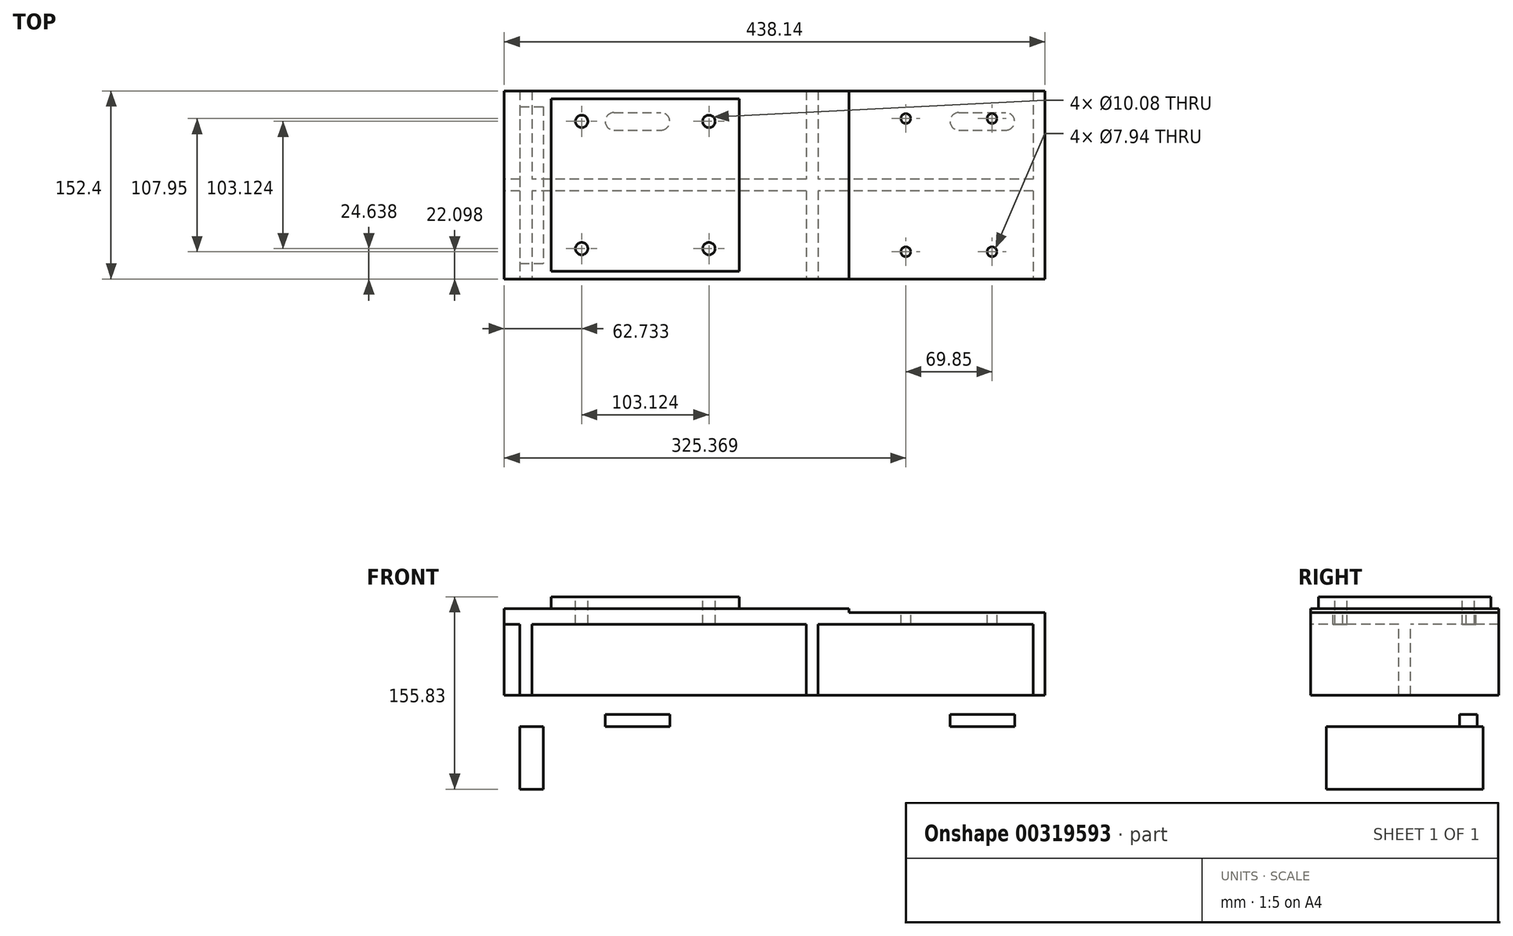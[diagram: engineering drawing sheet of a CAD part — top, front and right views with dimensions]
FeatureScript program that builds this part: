
annotation { "Feature Type Name" : "Feature", "Feature Type Description" : "" }
export const myFeature = defineFeature(function(context is Context, id is Id, definition is map)
    precondition{}
    {
        {
            var Q0;
            Q0=qCreatedBy(makeId("Top.planeOp"),FACE);
            var sketch = newSketch(context, id + "F0", { "sketchPlane" : qUnion([Q0])});
            skLineSegment(sketch, "E0.bottom", {"start": v(-219.08, 76.2) * mm, "end": v(219.08, 76.2) * mm});
            skLineSegment(sketch, "E0.top", {"start": v(-219.08, -76.2) * mm, "end": v(219.07, -76.2) * mm});
            skLineSegment(sketch, "E0.left", {"start": v(-219.08, 76.2) * mm, "end": v(-219.08, -76.2) * mm});
            skLineSegment(sketch, "E0.right", {"start": v(219.08, 76.2) * mm, "end": v(219.07, -76.2) * mm});
            skPoint(sketch, "E0.middle", {"position": v(0, 0) * mm});
            skSolve(sketch);
        }
        {
            var Q0;
            Q0 = qSketchRegion(id + "F0", true);
            extrude(context, id + "F1", {"entities" : qUnion([Q0]), "oppositeDirection" : true, "depth" : 12.7 * mm});
        }
        {
            var Q0;
            Q0=makeQuery(id+"F1.opExtrude","CAP_FACE",FACE,{"disambiguationData":[OSD([sQuery(id+"F0.wireOp",EDGE,"E0.bottom"),sQuery(id+"F0.wireOp",EDGE,"E0.top"),sQuery(id+"F0.wireOp",EDGE,"E0.left"),sQuery(id+"F0.wireOp",EDGE,"E0.right")])],"isStart":true});
            var sketch = newSketch(context, id + "F2", { "sketchPlane" : qUnion([Q0])});
            skLineSegment(sketch, "E1.0", {"start": v(-104.78, 76.2) * mm, "end": v(-104.78, -76.2) * mm, "construction": true});
            skLineSegment(sketch, "E2.bottom", {"start": v(-180.98, -69.85) * mm, "end": v(-28.58, -69.85) * mm});
            skLineSegment(sketch, "E2.top", {"start": v(-180.98, 69.85) * mm, "end": v(-28.58, 69.85) * mm});
            skLineSegment(sketch, "E2.left", {"start": v(-180.98, -69.85) * mm, "end": v(-180.98, 69.85) * mm});
            skLineSegment(sketch, "E2.right", {"start": v(-28.58, -69.85) * mm, "end": v(-28.58, 69.85) * mm});
            skPoint(sketch, "E2.middle", {"position": v(-104.78, 0) * mm});
            skSolve(sketch);
        }
        {
            var Q0;
            Q0 = qSketchRegion(id + "F2", true);
            extrude(context, id + "F3", {"entities" : qUnion([Q0]), "operationType" : NewBodyOperationType.ADD, "depth" : 9.52 * mm});
        }
        {
            var Q0;
            Q0=makeQuery(id+"F1.opExtrude","CAP_FACE",FACE,{"disambiguationData":[OSD([sQuery(id+"F0.wireOp",EDGE,"E0.bottom"),sQuery(id+"F0.wireOp",EDGE,"E0.top"),sQuery(id+"F0.wireOp",EDGE,"E0.left"),sQuery(id+"F0.wireOp",EDGE,"E0.right")])],"isStart":false});
            var sketch = newSketch(context, id + "F4", { "sketchPlane" : qUnion([Q0])});
            skLineSegment(sketch, "E3.0", {"start": v(-206.38, 76.2) * mm, "end": v(-196.72, 76.2) * mm});
            skLineSegment(sketch, "E4.0", {"start": v(-206.38, -76.2) * mm, "end": v(-196.72, -76.2) * mm});
            skLineSegment(sketch, "E5.0", {"start": v(-206.38, -76.2) * mm, "end": v(-206.38, 76.2) * mm});
            skLineSegment(sketch, "E6.0", {"start": v(-196.72, -76.2) * mm, "end": v(-196.72, 76.2) * mm});
            skLineSegment(sketch, "E7.0", {"start": v(25.53, -76.2) * mm, "end": v(25.53, 76.2) * mm});
            skLineSegment(sketch, "E8.0", {"start": v(35.18, -76.2) * mm, "end": v(35.18, 76.2) * mm});
            skLineSegment(sketch, "E9.0", {"start": v(219.08, -76.2) * mm, "end": v(219.07, 76.2) * mm});
            skLineSegment(sketch, "E10.0", {"start": v(209.42, -76.2) * mm, "end": v(209.42, 76.2) * mm});
            skLineSegment(sketch, "E11", {"start": v(219.08, 0) * mm, "end": v(-321.3, 0) * mm, "construction": true});
            skPoint(sketch, "E11.endSnap0", {"position": v(219.07, 0) * mm});
            skLineSegment(sketch, "E12.0", {"start": v(219.08, 4.76) * mm, "end": v(-219.08, 4.76) * mm});
            skLineSegment(sketch, "E13.MirrorCS", {"start": v(219.08, -4.76) * mm, "end": v(-219.08, -4.76) * mm});
            skLineSegment(sketch, "E14.0", {"start": v(-219.08, -4.76) * mm, "end": v(-219.08, 4.76) * mm});
            skPoint(sketch, "E15.orphan", {"position": v(-219.08, 76.2) * mm});
            skPoint(sketch, "E16.orphan", {"position": v(-321.3, 4.76) * mm});
            skPoint(sketch, "E17.orphan", {"position": v(-321.3, -4.76) * mm});
            skPoint(sketch, "E18.orphan", {"position": v(-219.08, -76.2) * mm});
            skLineSegment(sketch, "E19.trimOffspring", {"start": v(25.53, -76.2) * mm, "end": v(35.18, -76.2) * mm});
            skLineSegment(sketch, "E20.trimOffspring", {"start": v(25.53, 76.2) * mm, "end": v(35.18, 76.2) * mm});
            skLineSegment(sketch, "E21.trimOffspring", {"start": v(209.42, 76.2) * mm, "end": v(219.07, 76.2) * mm});
            skLineSegment(sketch, "E22.trimOffspring", {"start": v(209.42, -76.2) * mm, "end": v(219.08, -76.2) * mm});
            skSolve(sketch);
        }
        {
            var Q0;
            Q0 = qSketchRegion(id + "F4", true);
            extrude(context, id + "F5", {"entities" : qUnion([Q0]), "operationType" : NewBodyOperationType.ADD, "depth" : 73.15 * mm});
        }
        {
            var Q0;
            Q0=makeQuery(id+"F5.opExtrude","CAP_FACE",FACE,{"disambiguationData":[OSD([sQuery(id+"F4.wireOp",EDGE,"E3.0"),sQuery(id+"F4.wireOp",EDGE,"E4.0"),sQuery(id+"F4.wireOp",EDGE,"E5.0"),sQuery(id+"F4.wireOp",EDGE,"E6.0"),sQuery(id+"F4.wireOp",EDGE,"E7.0"),sQuery(id+"F4.wireOp",EDGE,"E8.0"),sQuery(id+"F4.wireOp",EDGE,"E9.0"),sQuery(id+"F4.wireOp",EDGE,"E10.0"),sQuery(id+"F4.wireOp",EDGE,"E12.0"),sQuery(id+"F4.wireOp",EDGE,"E13.MirrorCS"),sQuery(id+"F4.wireOp",EDGE,"E14.0"),sQuery(id+"F4.wireOp",EDGE,"E19.trimOffspring"),sQuery(id+"F4.wireOp",EDGE,"E20.trimOffspring"),sQuery(id+"F4.wireOp",EDGE,"E21.trimOffspring"),sQuery(id+"F4.wireOp",EDGE,"E22.trimOffspring")])],"isStart":false});
            var sketch = newSketch(context, id + "F6", { "sketchPlane" : qUnion([Q0])});
            skLineSegment(sketch, "E23.0", {"start": v(-219.08, 76.2) * mm, "end": v(219.07, 76.2) * mm});
            skLineSegment(sketch, "E24.0", {"start": v(-219.08, -76.2) * mm, "end": v(-219.08, 76.2) * mm});
            skLineSegment(sketch, "E25.0", {"start": v(-219.08, -76.2) * mm, "end": v(219.08, -76.2) * mm});
            skLineSegment(sketch, "E26.0", {"start": v(219.08, -76.2) * mm, "end": v(219.07, 76.2) * mm});
            skPoint(sketch, "E27.orphan", {"position": v(-219.08, -4.76) * mm});
            skPoint(sketch, "E28.orphan", {"position": v(-196.72, 76.2) * mm});
            skPoint(sketch, "E29.orphan", {"position": v(25.53, 76.2) * mm});
            skPoint(sketch, "E30.orphan", {"position": v(-196.72, -76.2) * mm});
            skPoint(sketch, "E31.orphan", {"position": v(25.53, -76.2) * mm});
            skSolve(sketch);
        }
        {
            var Q0;
            Q0 = qSketchRegion(id + "F6", true);
            extrude(context, id + "F7", {"entities" : qUnion([Q0]), "operationType" : NewBodyOperationType.ADD, "depth" : 9.65 * mm});
        }
        {
            var Q0;
            Q0=makeQuery(id+"F7.opExtrude","CAP_FACE",FACE,{"disambiguationData":[OSD([sQuery(id+"F6.wireOp",EDGE,"E23.0"),sQuery(id+"F6.wireOp",EDGE,"E24.0"),sQuery(id+"F6.wireOp",EDGE,"E25.0"),sQuery(id+"F6.wireOp",EDGE,"E26.0")])],"isStart":false});
            var sketch = newSketch(context, id + "F8", { "sketchPlane" : qUnion([Q0])});
            skLineSegment(sketch, "E32", {"start": v(-219.08, 0) * mm, "end": v(219.07, 0) * mm, "construction": true});
            skLineSegment(sketch, "E33.0", {"start": v(-130.18, -76.2) * mm, "end": v(-130.18, 76.2) * mm, "construction": true});
            skLineSegment(sketch, "E34.0", {"start": v(-92.08, -76.2) * mm, "end": v(-92.08, 76.2) * mm, "construction": true});
            skLineSegment(sketch, "E35.0", {"start": v(149.22, -76.2) * mm, "end": v(149.22, 76.2) * mm, "construction": true});
            skLineSegment(sketch, "E36.0", {"start": v(187.32, -76.2) * mm, "end": v(187.32, 76.2) * mm, "construction": true});
            skLineSegment(sketch, "E37.0", {"start": v(-130.18, -51.56) * mm, "end": v(-92.08, -51.56) * mm});
            skLineSegment(sketch, "E38.trimOffspring", {"start": v(149.22, -51.56) * mm, "end": v(187.32, -51.56) * mm});
            skArc(sketch, "E39.0.startCap", {"start": v(-130.18, -58.67) * mm, "mid": v(-137.29, -51.56) * mm, "end": v(-130.18, -44.45) * mm});
            skArc(sketch, "E39.0.endCap", {"start": v(-92.08, -44.45) * mm, "mid": v(-84.96, -51.56) * mm, "end": v(-92.08, -58.67) * mm});
            skLineSegment(sketch, "E39.0.left", {"start": v(-130.18, -44.45) * mm, "end": v(-92.08, -44.45) * mm});
            skLineSegment(sketch, "E39.0.right", {"start": v(-130.18, -58.67) * mm, "end": v(-92.08, -58.67) * mm});
            skArc(sketch, "E39.1.startCap", {"start": v(149.22, -58.67) * mm, "mid": v(142.11, -51.56) * mm, "end": v(149.22, -44.45) * mm});
            skArc(sketch, "E39.1.endCap", {"start": v(187.32, -44.45) * mm, "mid": v(194.44, -51.56) * mm, "end": v(187.32, -58.67) * mm});
            skLineSegment(sketch, "E39.1.left", {"start": v(149.22, -44.45) * mm, "end": v(187.32, -44.45) * mm});
            skLineSegment(sketch, "E39.1.right", {"start": v(149.22, -58.67) * mm, "end": v(187.32, -58.67) * mm});
            skArc(sketch, "E40.MirrorCS", {"start": v(-92.08, 44.45) * mm, "mid": v(-84.96, 51.56) * mm, "end": v(-92.08, 58.67) * mm});
            skArc(sketch, "E41.MirrorCS", {"start": v(-130.18, 58.67) * mm, "mid": v(-137.29, 51.56) * mm, "end": v(-130.18, 44.45) * mm});
            skLineSegment(sketch, "E42.MirrorCS", {"start": v(149.22, 51.56) * mm, "end": v(187.32, 51.56) * mm});
            skLineSegment(sketch, "E43.MirrorCS", {"start": v(-130.18, 51.56) * mm, "end": v(-92.08, 51.56) * mm});
            skLineSegment(sketch, "E44.MirrorCS", {"start": v(149.22, 58.67) * mm, "end": v(187.32, 58.67) * mm});
            skLineSegment(sketch, "E45.MirrorCS", {"start": v(-130.18, 44.45) * mm, "end": v(-92.08, 44.45) * mm});
            skLineSegment(sketch, "E46.MirrorCS", {"start": v(149.22, 44.45) * mm, "end": v(187.32, 44.45) * mm});
            skArc(sketch, "E47.MirrorCS", {"start": v(149.22, 58.67) * mm, "mid": v(142.11, 51.56) * mm, "end": v(149.22, 44.45) * mm});
            skArc(sketch, "E48.MirrorCS", {"start": v(187.32, 44.45) * mm, "mid": v(194.44, 51.56) * mm, "end": v(187.32, 58.67) * mm});
            skLineSegment(sketch, "E49.MirrorCS", {"start": v(-130.18, 58.67) * mm, "end": v(-92.08, 58.67) * mm});
            skSolve(sketch);
        }
        {
            var Q0;
            Q0=makeQuery(id+"F8.imprint","IMPRINT",FACE,{"disambiguationData":[TD([[makeQuery(id+"F8.imprint","IMPRINT",EDGE,{"derivedFrom":sQuery(id+"F8.wireOp",EDGE,"E40.MirrorCS")}),1.0]])]});
            var Q1;
            Q1=makeQuery(id+"F8.imprint","IMPRINT",FACE,{"disambiguationData":[TD([[makeQuery(id+"F8.imprint","IMPRINT",EDGE,{"derivedFrom":sQuery(id+"F8.wireOp",EDGE,"E39.0.startCap")}),-1.0]])]});
            var Q2;
            Q2=makeQuery(id+"F8.imprint","IMPRINT",FACE,{"disambiguationData":[TD([[makeQuery(id+"F8.imprint","IMPRINT",EDGE,{"derivedFrom":sQuery(id+"F8.wireOp",EDGE,"E44.MirrorCS")}),-1.0]])]});
            var Q3;
            Q3=makeQuery(id+"F8.imprint","IMPRINT",FACE,{"disambiguationData":[TD([[makeQuery(id+"F8.imprint","IMPRINT",EDGE,{"derivedFrom":sQuery(id+"F8.wireOp",EDGE,"E39.1.startCap")}),-1.0]])]});
            extrude(context, id + "F9", {"entities" : qUnion([Q0, Q1, Q2, Q3]), "operationType" : NewBodyOperationType.REMOVE, "oppositeDirection" : true, "depth" : 25.4 * mm});
        }
        {
            var Q0;
            Q0=makeQuery(id+"F3.opExtrude","CAP_FACE",FACE,{"disambiguationData":[OSD([sQuery(id+"F2.wireOp",EDGE,"E2.bottom"),sQuery(id+"F2.wireOp",EDGE,"E2.top"),sQuery(id+"F2.wireOp",EDGE,"E2.left"),sQuery(id+"F2.wireOp",EDGE,"E2.right")])],"isStart":false});
            var sketch = newSketch(context, id + "F10", { "sketchPlane" : qUnion([Q0])});
            skLineSegment(sketch, "E50.0", {"start": v(-180.98, 69.85) * mm, "end": v(-28.58, 69.85) * mm, "construction": true});
            skLineSegment(sketch, "E51.0", {"start": v(-180.98, -69.85) * mm, "end": v(-180.98, 69.85) * mm, "construction": true});
            skLineSegment(sketch, "E52.0", {"start": v(-180.98, -69.85) * mm, "end": v(-28.58, -69.85) * mm, "construction": true});
            skLineSegment(sketch, "E53", {"start": v(-28.58, -69.85) * mm, "end": v(-180.97, 69.85) * mm, "construction": true});
            skLineSegment(sketch, "E54.bottom", {"start": v(-156.34, 51.56) * mm, "end": v(-53.21, 51.56) * mm, "construction": true});
            skLineSegment(sketch, "E54.top", {"start": v(-156.34, -51.56) * mm, "end": v(-53.21, -51.56) * mm, "construction": true});
            skLineSegment(sketch, "E54.left", {"start": v(-156.34, 51.56) * mm, "end": v(-156.34, -51.56) * mm, "construction": true});
            skLineSegment(sketch, "E54.right", {"start": v(-53.21, 51.56) * mm, "end": v(-53.21, -51.56) * mm, "construction": true});
            skPoint(sketch, "E54.middle", {"position": v(-104.78, 0) * mm});
            skPoint(sketch, "E55", {"position": v(-156.34, 51.56) * mm});
            skPoint(sketch, "E56", {"position": v(-53.21, 51.56) * mm});
            skPoint(sketch, "E57", {"position": v(-156.34, -51.56) * mm});
            skPoint(sketch, "E58", {"position": v(-53.21, -51.56) * mm});
            skSolve(sketch);
        }
        {
            var Q0;
            Q0=sQuery(id+"F10.wireOp",VERTEX,"E55");
            var Q1;
            Q1=sQuery(id+"F10.wireOp",VERTEX,"E56");
            var Q2;
            Q2=sQuery(id+"F10.wireOp",VERTEX,"E57");
            var Q3;
            Q3=sQuery(id+"F10.wireOp",VERTEX,"E58");
            var Q4;
            Q4=makeQuery(id+"F1.opExtrude","SWEPT_BODY",BODY,{"disambiguationData":[OSD([sQuery(id+"F0.wireOp",EDGE,"E0.bottom"),sQuery(id+"F0.wireOp",EDGE,"E0.top"),sQuery(id+"F0.wireOp",EDGE,"E0.left"),sQuery(id+"F0.wireOp",EDGE,"E0.right")])]});
            hole(context, id + "F11", {"style" : HoleStyle.SIMPLE, "endStyle" : HoleEndStyle.BLIND, "standardTappedOrClearance" : lookupTablePath({ "standard" : "ANSI", "fit" : "Normal (ASME)", "size" : "3/8", "type" : "Clearance" }), "standardBlindInLast" : lookupTablePath({ "fit" : "Free", "standard" : "ANSI", "size" : "3/8", "type" : "Clearance" }), "holeDiameter" : 10.08 * mm, "holeDepth" : 38.1 * mm, "tappedDepth" : 14.3 * mm, "tapClearance" : 3, "locations" : qUnion([Q0, Q1, Q2, Q3]), "scope" : qUnion([Q4])});
        }
        {
            var Q0;
            Q0=makeQuery(id+"F1.opExtrude","CAP_FACE",FACE,{"disambiguationData":[OSD([sQuery(id+"F0.wireOp",EDGE,"E0.bottom"),sQuery(id+"F0.wireOp",EDGE,"E0.top"),sQuery(id+"F0.wireOp",EDGE,"E0.left"),sQuery(id+"F0.wireOp",EDGE,"E0.right")])],"isStart":true});
            var sketch = newSketch(context, id + "F12", { "sketchPlane" : qUnion([Q0])});
            skLineSegment(sketch, "E59.bottom", {"start": v(219.08, 76.2) * mm, "end": v(60.33, 76.2) * mm});
            skLineSegment(sketch, "E59.top", {"start": v(219.08, -76.2) * mm, "end": v(60.33, -76.2) * mm});
            skLineSegment(sketch, "E59.left", {"start": v(219.08, 76.2) * mm, "end": v(219.08, -76.2) * mm});
            skLineSegment(sketch, "E59.right", {"start": v(60.33, 76.2) * mm, "end": v(60.33, -76.2) * mm});
            skSolve(sketch);
        }
        {
            var Q0;
            Q0 = qSketchRegion(id + "F12", true);
            extrude(context, id + "F13", {"entities" : qUnion([Q0]), "operationType" : NewBodyOperationType.REMOVE, "oppositeDirection" : true, "depth" : 3.17 * mm});
        }
        {
            var Q0;
            Q0=makeQuery(id+"F13.boolean.opBoolean","COPY",FACE,{"derivedFrom":makeQuery(id+"F13.opExtrude","CAP_FACE",FACE,{"disambiguationData":[OSD([sQuery(id+"F12.wireOp",EDGE,"E59.bottom"),sQuery(id+"F12.wireOp",EDGE,"E59.top"),sQuery(id+"F12.wireOp",EDGE,"E59.left"),sQuery(id+"F12.wireOp",EDGE,"E59.right")])],"isStart":false})});
            var sketch = newSketch(context, id + "F14", { "sketchPlane" : qUnion([Q0])});
            skLineSegment(sketch, "E60.0", {"start": v(-180.98, 69.85) * mm, "end": v(-28.58, 69.85) * mm, "construction": true});
            skLineSegment(sketch, "E61", {"start": v(-104.78, 69.85) * mm, "end": v(-104.78, -100.76) * mm, "construction": true});
            skLineSegment(sketch, "E62.0", {"start": v(219.08, 76.2) * mm, "end": v(219.07, -76.2) * mm, "construction": true});
            skLineSegment(sketch, "E63", {"start": v(219.07, 0) * mm, "end": v(-246.08, 0) * mm, "construction": true});
            skLineSegment(sketch, "E64.0", {"start": v(141.35, 69.85) * mm, "end": v(141.35, -100.76) * mm, "construction": true});
            skLineSegment(sketch, "E65.0", {"start": v(106.3, 69.85) * mm, "end": v(106.3, -100.76) * mm, "construction": true});
            skLineSegment(sketch, "E66.0", {"start": v(219.07, 53.85) * mm, "end": v(-246.08, 53.85) * mm, "construction": true});
            skPoint(sketch, "E67", {"position": v(106.3, 53.85) * mm});
            skPoint(sketch, "E68.0.1.0", {"position": v(106.3, -54.1) * mm});
            skPoint(sketch, "E68.1.0.0", {"position": v(176.15, 53.85) * mm});
            skPoint(sketch, "E68.1.1.0", {"position": v(176.15, -54.1) * mm});
            skLineSegment(sketch, "E68.direction1", {"start": v(106.3, 53.85) * mm, "end": v(176.15, 53.85) * mm, "construction": true});
            skLineSegment(sketch, "E68.direction2", {"start": v(106.3, 53.85) * mm, "end": v(106.3, -54.1) * mm, "construction": true});
            skSolve(sketch);
        }
        {
            var Q0;
            Q0=sQuery(id+"F14.wireOp",VERTEX,"E67");
            var Q1;
            Q1=sQuery(id+"F14.wireOp",VERTEX,"E68.1.0.0");
            var Q2;
            Q2=sQuery(id+"F14.wireOp",VERTEX,"E68.1.1.0");
            var Q3;
            Q3=sQuery(id+"F14.wireOp",VERTEX,"E68.0.1.0");
            var Q4;
            Q4=makeQuery(id+"F1.opExtrude","SWEPT_BODY",BODY,{"disambiguationData":[OSD([sQuery(id+"F0.wireOp",EDGE,"E0.bottom"),sQuery(id+"F0.wireOp",EDGE,"E0.top"),sQuery(id+"F0.wireOp",EDGE,"E0.left"),sQuery(id+"F0.wireOp",EDGE,"E0.right")])]});
            hole(context, id + "F15", {"style" : HoleStyle.SIMPLE, "endStyle" : HoleEndStyle.BLIND, "holeDiameter" : 7.94 * mm, "holeDepth" : 38.1 * mm, "tappedDepth" : 14.3 * mm, "tapClearance" : 3, "locations" : qUnion([Q0, Q1, Q2, Q3]), "scope" : qUnion([Q4])});
        }
        {
            var Q0;
            Q0=makeQuery(id+"F7.opExtrude","CAP_FACE",FACE,{"disambiguationData":[OSD([sQuery(id+"F6.wireOp",EDGE,"E23.0"),sQuery(id+"F6.wireOp",EDGE,"E24.0"),sQuery(id+"F6.wireOp",EDGE,"E25.0"),sQuery(id+"F6.wireOp",EDGE,"E26.0")])],"isStart":false});
            var sketch = newSketch(context, id + "F16", { "sketchPlane" : qUnion([Q0])});
            skLineSegment(sketch, "E69.0", {"start": v(-206.38, -63.5) * mm, "end": v(-206.38, 63.5) * mm});
            skLineSegment(sketch, "E70.0", {"start": v(-187.33, -63.5) * mm, "end": v(-187.33, 63.5) * mm});
            skLineSegment(sketch, "E71", {"start": v(-219.08, 0) * mm, "end": v(-163.17, 0) * mm, "construction": true});
            skPoint(sketch, "E71.endSnap0", {"position": v(-219.08, 0) * mm});
            skLineSegment(sketch, "E72.0", {"start": v(-206.38, -63.5) * mm, "end": v(-187.33, -63.5) * mm});
            skLineSegment(sketch, "E73.MirrorCS", {"start": v(-206.38, 63.5) * mm, "end": v(-187.33, 63.5) * mm});
            skPoint(sketch, "E74.orphan", {"position": v(-219.08, 63.5) * mm});
            skPoint(sketch, "E75.orphan", {"position": v(-163.17, 63.5) * mm});
            skPoint(sketch, "E76.orphan", {"position": v(-163.17, -63.5) * mm});
            skPoint(sketch, "E77.orphan", {"position": v(-219.08, -63.5) * mm});
            skSolve(sketch);
        }
        {
            var Q0;
            Q0 = qSketchRegion(id + "F16", true);
            extrude(context, id + "F17", {"entities" : qUnion([Q0]), "operationType" : NewBodyOperationType.ADD, "depth" : 50.8 * mm});
        }
        {
            var Q0;
            Q0=makeQuery(id+"F17.opExtrude","SWEPT_FACE",FACE,{"disambiguationData":[OSD([sQuery(id+"F16.wireOp",EDGE,"E69.0")])]});
            var sketch = newSketch(context, id + "F18", { "sketchPlane" : qUnion([Q0])});
            skLineSegment(sketch, "E78.0", {"start": v(-76.2, -127.25) * mm, "end": v(76.2, -127.25) * mm, "construction": true});
            skLineSegment(sketch, "E79", {"start": v(0, -146.3) * mm, "end": v(0, -111.54) * mm, "construction": true});
            skPoint(sketch, "E79.endSnap0", {"position": v(0, -127.25) * mm});
            skLineSegment(sketch, "E80.0", {"start": v(50.8, -146.3) * mm, "end": v(50.8, -111.54) * mm, "construction": true});
            skPoint(sketch, "E81", {"position": v(50.8, -127.25) * mm});
            skPoint(sketch, "E82.MirrorP", {"position": v(-50.8, -127.25) * mm});
            skSolve(sketch);
        }
        {
            var Q0;
            Q0=sQuery(id+"F18.wireOp",VERTEX,"E81");
            var Q1;
            Q1=sQuery(id+"F18.wireOp",VERTEX,"E82.MirrorP");
            var Q2;
            Q2=makeQuery(id+"F1.opExtrude","SWEPT_BODY",BODY,{"disambiguationData":[OSD([sQuery(id+"F0.wireOp",EDGE,"E0.bottom"),sQuery(id+"F0.wireOp",EDGE,"E0.top"),sQuery(id+"F0.wireOp",EDGE,"E0.left"),sQuery(id+"F0.wireOp",EDGE,"E0.right")])]});
            hole(context, id + "F19", {"style" : HoleStyle.SIMPLE, "endStyle" : HoleEndStyle.BLIND, "standardTappedOrClearance" : lookupTablePath({ "standard" : "ANSI", "engagement" : "75%", "pitch" : "11 tpi", "size" : "5/8", "type" : "Tapped" }), "standardBlindInLast" : lookupTablePath({ "standard" : "ANSI", "engagement" : "75%", "pitch" : "11 tpi", "size" : "5/8", "type" : "Tapped" }), "holeDiameter" : 13.5 * mm, "showTappedDepth" : true, "holeDepth" : 21.23 * mm, "tappedDepth" : 14.3 * mm, "tapClearance" : 3, "locations" : qUnion([Q0, Q1]), "scope" : qUnion([Q2]), "majorDiameter" : 15.88 * mm});
        }
    });
